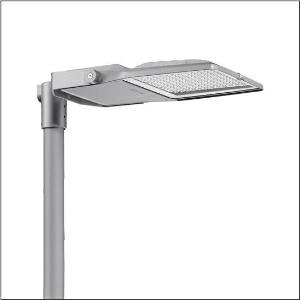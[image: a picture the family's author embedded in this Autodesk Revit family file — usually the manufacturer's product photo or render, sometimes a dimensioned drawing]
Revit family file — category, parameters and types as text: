
# Revit family: floodlight_fl_21_midi___pl64_5xa7785f2e3a_d9f8
name_source: partatom
category: Lighting Fixtures
units: mm (PartAtom-declared; Revit-internal decimal feet)

## family parameters
Cut with Voids When Loaded = No
Host = Face
Light Source = No
Part Type = Normal
Room Calculation Point = No
Round Connector Dimension = Use Diameter
Shared = No

## types (1)
- --- (1 x LED, 34530 lm, 271.6 W, 3000K)
    Apparent Load = 272 VA
    CIE Flux Codes = 28 80 98 100 100
    Color Rendering = 70
    Color Temperature = 3000K
    Default Elevation = 1800 mm
    Description = Floodlight FL 21 midi, floodlight, primary light control with lens, of PMMA, primary optical cover: protective disc, of toughened safety glass, transparent, light distribution: PL64, light emission: direct distribution, installation type: surface-mounted, LED, High Power LED, rated luminous flux: 34.530lm, luminous efficacy: 127lm/W, light colour: 730, colour temperature: 3000K, control gear: ECG Smart Interface, control: flexible luminous flux parameterisation, time-dependent luminous flux control, constant luminous flux control, overheat protection, pre-setting: logarithmic dimming characteristic, with terminal, 6-pole, mains connection: 220..240V, AC, 50/60Hz, start of lifetime: 272W, end of service life: 287W, reduction: 123W, luminaire housing, of diecast aluminium, powder-coated, Siteco® metallic grey (DB 702S), sealing non-destructively replaceable, please order mast flange separately, mast bracket, of steel, galvanised, powder-coated, Siteco® metallic grey (DB 702S), Smart Interface above, protection rating (complete): IP66, insulation class (complete): insulation class II (safety insulation), certification: CE, ENEC, VDE, protection symbol: D, impact resistance: IK08, permissible operating ambient temperature: -40..+40°C, permissible operating ambient temperature for outdoor applications: -40..+50°C, standard: DIN EN 12944, LABS conformity tested according to VDMA 24364:2018-05, packaging unit: 1 piece

Light Distribution: PL64
    Height = 76 mm
    Lamp = 1 x LED
    Lamp Light Flux = 34530 lm
    Lamp Power = 271.6 W
    Lamp count = 1
    Length = 657 mm
    Luminous efficacy = 127 lm/W
    Manufacturer = Siteco
    ModVariant = No
    Model = 5XA7785F2E3A
    Number of Poles = 1
    OnlyDefault = Yes
    Power Factor = 1
    Product Name = Floodlight FL 21 midi | PL64
    Product group = floodlight | pylon annexe
    ProductGroupID = 6200
    Protection Class = Protection class II
    Protection Degree = IP 66
    RLX_Detail_Level = 1
    RLX_Emergency_Light_Flux = 0 lm
    RLX_Emergency_Type = 0
    RLX_Emergency_Type_DB = No
    RlxData = <blob elided: 153617 chars, md5=a89585ff>
    Socket = socket
    Standby Power = 0 W
    System Light Flux = 34530 lm
    System Power = 272 W
    Type Comments = factory setting: luminous flux: 100 % | dim-lin: 254 | 620 mA
    Type Image = l_1007123.jpg
    URL = http://relux.com
    VarID = @adj_151779
    Voltage = 0 V
    Weight = 0.00 kg
    Width = 442 mm

## geometry (parser evidence)
native form markers: Blend x4, Sweep x14
no freeform markers — native parametric forms only
